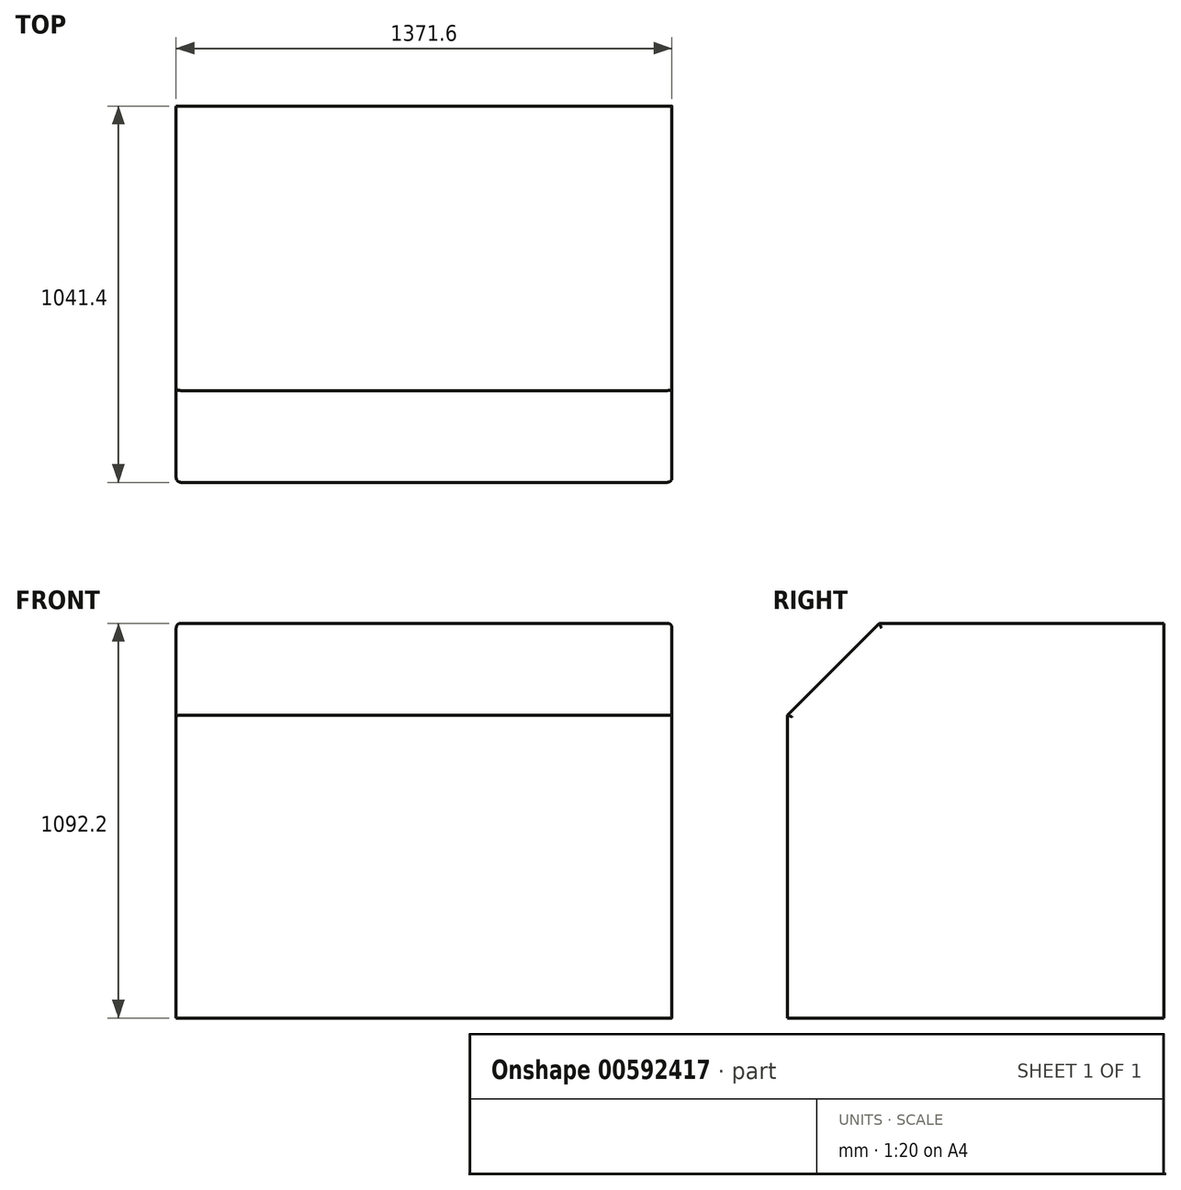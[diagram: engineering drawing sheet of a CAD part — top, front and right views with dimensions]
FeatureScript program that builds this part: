
annotation { "Feature Type Name" : "Feature", "Feature Type Description" : "" }
export const myFeature = defineFeature(function(context is Context, id is Id, definition is map)
    precondition{}
    {
        {
            var Q0;
            Q0=qCreatedBy(makeId("Top.planeOp"),FACE);
            var sketch = newSketch(context, id + "F0", { "sketchPlane" : qUnion([Q0])});
            skLineSegment(sketch, "E0.bottom", {"start": v(685.8, -520.7) * mm, "end": v(-685.8, -520.7) * mm});
            skLineSegment(sketch, "E0.top", {"start": v(685.8, 520.7) * mm, "end": v(-685.8, 520.7) * mm});
            skLineSegment(sketch, "E0.left", {"start": v(685.8, -520.7) * mm, "end": v(685.8, 520.7) * mm});
            skLineSegment(sketch, "E0.right", {"start": v(-685.8, -520.7) * mm, "end": v(-685.8, 520.7) * mm});
            skPoint(sketch, "E0.middle", {"position": v(0, 0) * mm});
            skSolve(sketch);
        }
        {
            var Q0;
            Q0=makeQuery(id+"F0.imprint","IMPRINT",FACE,{"disambiguationData":[TD([[makeQuery(id+"F0.imprint","IMPRINT",EDGE,{"derivedFrom":sQuery(id+"F0.wireOp",EDGE,"E0.bottom")}),-1.0]])]});
            extrude(context, id + "F1", {"entities" : qUnion([Q0]), "depth" : 1092.2 * mm, "offsetDistance" : 25.4 * mm});
        }
        {
            var Q0;
            Q0=makeQuery(id+"F1.opExtrude","CAP_EDGE",EDGE,{"disambiguationData":[OSD([sQuery(id+"F0.wireOp",EDGE,"E0.bottom")])],"isStart":false});
            chamfer(context, id + "F2", {"entities" : qUnion([Q0]), "width" : 254 * mm, "tangentPropagation" : true});
        }
        {
            var Q0;
            Q0=makeQuery(id+"F1.opExtrude","CAP_EDGE",EDGE,{"disambiguationData":[OSD([sQuery(id+"F0.wireOp",EDGE,"E0.left")])],"isStart":false});
            var Q1;
            Q1=makeQuery(id+"F2.opChamfer","BLEND_EDGE",EDGE,{"blendedFrom":[makeQuery(id+"F1.opExtrude","CAP_EDGE",EDGE,{"disambiguationData":[OSD([sQuery(id+"F0.wireOp",EDGE,"E0.bottom")])],"isStart":false}),makeQuery(id+"F1.opExtrude","SWEPT_FACE",FACE,{"disambiguationData":[OSD([sQuery(id+"F0.wireOp",EDGE,"E0.left")])]})],"blendedInto":[makeQuery(id+"F1.opExtrude","SWEPT_FACE",FACE,{"disambiguationData":[OSD([sQuery(id+"F0.wireOp",EDGE,"E0.left")])]})]});
            var Q2;
            Q2=makeQuery(id+"F1.opExtrude","SWEPT_EDGE",EDGE,{"disambiguationData":[OSD([sQuery(id+"F0.wireOp",EDGE,"E0.bottom"),sQuery(id+"F0.wireOp",EDGE,"E0.left")])]});
            var Q3;
            Q3=makeQuery(id+"F1.opExtrude","CAP_EDGE",EDGE,{"disambiguationData":[OSD([sQuery(id+"F0.wireOp",EDGE,"E0.right")])],"isStart":false});
            var Q4;
            Q4=makeQuery(id+"F2.opChamfer","BLEND_EDGE",EDGE,{"blendedFrom":[makeQuery(id+"F1.opExtrude","CAP_EDGE",EDGE,{"disambiguationData":[OSD([sQuery(id+"F0.wireOp",EDGE,"E0.bottom")])],"isStart":false}),makeQuery(id+"F1.opExtrude","SWEPT_FACE",FACE,{"disambiguationData":[OSD([sQuery(id+"F0.wireOp",EDGE,"E0.right")])]})],"blendedInto":[makeQuery(id+"F1.opExtrude","SWEPT_FACE",FACE,{"disambiguationData":[OSD([sQuery(id+"F0.wireOp",EDGE,"E0.right")])]})]});
            var Q5;
            Q5=makeQuery(id+"F1.opExtrude","SWEPT_EDGE",EDGE,{"disambiguationData":[OSD([sQuery(id+"F0.wireOp",EDGE,"E0.bottom"),sQuery(id+"F0.wireOp",EDGE,"E0.right")])]});
            fillet(context, id + "F3", {"entities" : qUnion([Q0, Q1, Q2, Q3, Q4, Q5]), "radius" : 12.7 * mm, "tangentPropagation" : true, "allowEdgeOverflow" : false});
        }
    });
